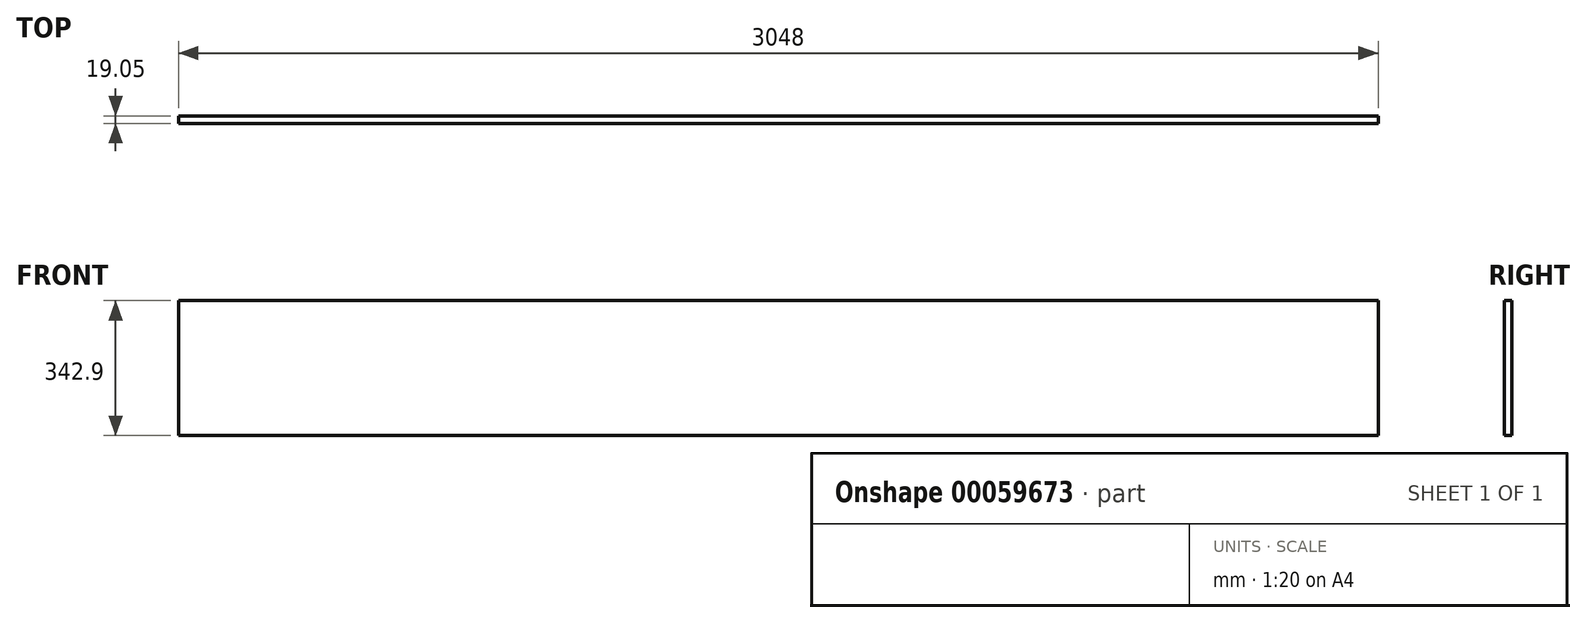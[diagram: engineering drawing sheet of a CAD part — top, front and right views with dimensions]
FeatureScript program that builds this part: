
annotation { "Feature Type Name" : "Feature", "Feature Type Description" : "" }
export const myFeature = defineFeature(function(context is Context, id is Id, definition is map)
    precondition{}
    {
        {
            var Q0;
            Q0=qCreatedBy(makeId("Front.planeOp"),FACE);
            var sketch = newSketch(context, id + "F0", { "sketchPlane" : qUnion([Q0])});
            skLineSegment(sketch, "E0.bottom", {"start": v(0, 0) * mm, "end": v(3048, 0) * mm});
            skLineSegment(sketch, "E0.top", {"start": v(0, 342.9) * mm, "end": v(3048, 342.9) * mm});
            skLineSegment(sketch, "E0.left", {"start": v(0, 0) * mm, "end": v(0, 342.9) * mm});
            skLineSegment(sketch, "E0.right", {"start": v(3048, 0) * mm, "end": v(3048, 342.9) * mm});
            skSolve(sketch);
        }
        {
            var Q0;
            Q0=makeQuery(id+"F0.imprint","IMPRINT",FACE,{"disambiguationData":[TD([[makeQuery(id+"F0.imprint","IMPRINT",EDGE,{"derivedFrom":sQuery(id+"F0.wireOp",EDGE,"E0.bottom")}),1.0]])]});
            extrude(context, id + "F1", {"entities" : qUnion([Q0]), "depth" : 19.05 * mm});
        }
    });
